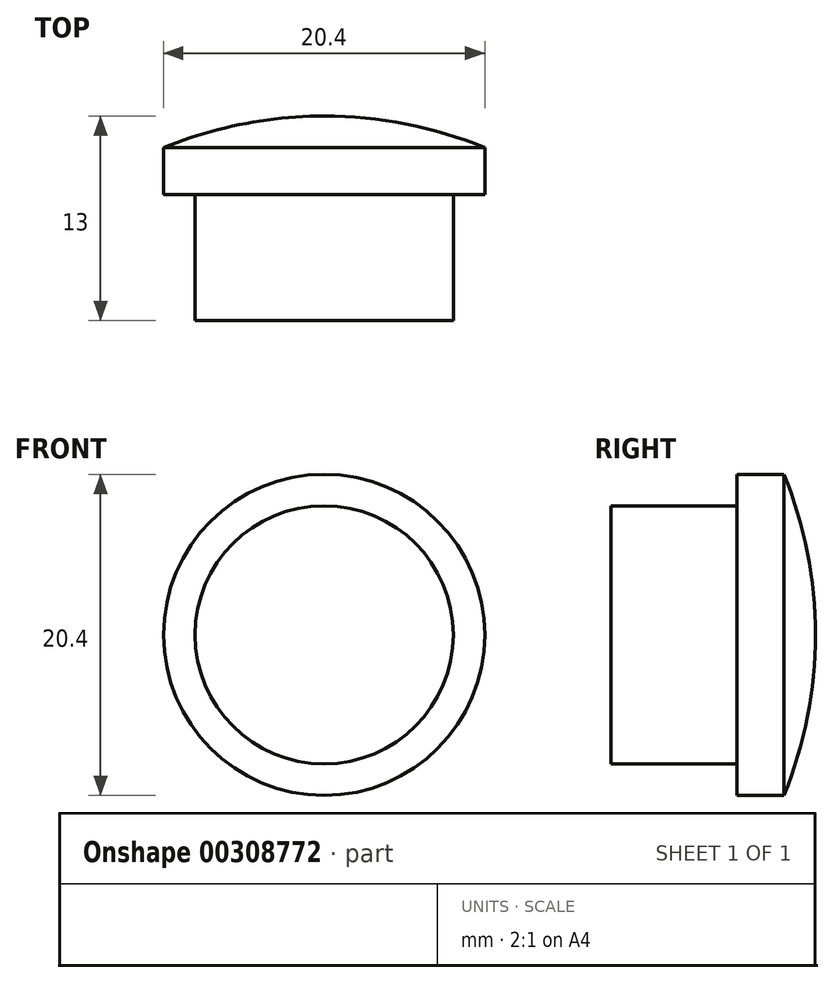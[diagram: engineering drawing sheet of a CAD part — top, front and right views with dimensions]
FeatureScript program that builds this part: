
annotation { "Feature Type Name" : "Feature", "Feature Type Description" : "" }
export const myFeature = defineFeature(function(context is Context, id is Id, definition is map)
    precondition{}
    {
        {
            var Q0;
            Q0=qCreatedBy(makeId("Top.planeOp"),FACE);
            var sketch = newSketch(context, id + "F0", { "sketchPlane" : qUnion([Q0])});
            skLineSegment(sketch, "E0", {"start": v(0, 0) * mm, "end": v(-8.2, 0) * mm});
            skLineSegment(sketch, "E1", {"start": v(-8.2, 0) * mm, "end": v(-8.2, 8) * mm});
            skLineSegment(sketch, "E2", {"start": v(-8.2, 8) * mm, "end": v(-10.2, 8) * mm});
            skLineSegment(sketch, "E3", {"start": v(0, -13) * mm, "end": v(0, 0) * mm});
            skLineSegment(sketch, "E4", {"start": v(0, 13) * mm, "end": v(0, -13) * mm});
            skLineSegment(sketch, "E5", {"start": v(-10.2, 8) * mm, "end": v(-10.2, 11) * mm});
            skArc(sketch, "E6", {"start": v(0, 13) * mm, "mid": v(-5.2, 12.5) * mm, "end": v(-10.2, 11) * mm});
            skSolve(sketch);
        }
        {
            var Q0;
            Q0=makeQuery(id+"F0.imprint","IMPRINT",FACE,{"disambiguationData":[TD([[makeQuery(id+"F0.imprint","IMPRINT",EDGE,{"derivedFrom":sQuery(id+"F0.wireOp",EDGE,"E0")}),-1.0]])]});
            var Q1;
            Q1=sQuery(id+"F0.wireOp",EDGE,"E3");
            revolve(context, id + "F1", {"entities" : qUnion([Q0]), "axis" : qUnion([Q1]), "revolveType" : RevolveType.FULL});
        }
    });
